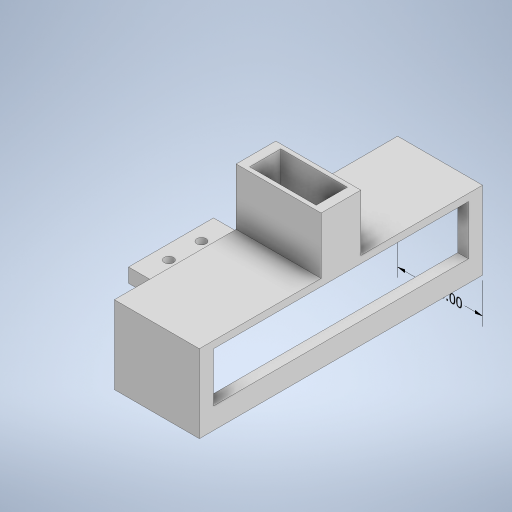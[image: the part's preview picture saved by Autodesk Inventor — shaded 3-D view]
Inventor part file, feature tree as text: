
AUTODESK INVENTOR PART (.ipt)
format: ipt  version: 2023 (Build 270158000, 158)  size: 323,584 bytes
history: native  units: mm
features: extrude x8, sketch x8, other x3, plane x1
ambient origin geometry x8: Origin, YZ Plane, XZ Plane, XY Plane, X Axis, Y Axis, Z Axis, Center Point
bodies: Body1 (feature_tree)
feature tree (20):
  other  "Sólido1"
  other  "Anotaciones"
  extrude  "Extrusión1"  Depth=200.0mm
  extrude  "Extrusión2"  Depth=45.0mm
  extrude  "Extrusión3"  TaperAngle=0.0deg  [1 undecoded]
  extrude  "Extrusión4"  Depth=10.0mm
  extrude  "Extrusión5"  Depth=10.0mm TaperAngle=0.0deg
  extrude  "Extrusión6"  Depth=60.0mm
  extrude  "Extrusión7"  Depth=6.5mm
  plane  "Plano de trabajo1"
  extrude  "Extrusión8"  Depth=18.5mm
  sketch  "Boceto2"  dims[d0=60.0mm d1=200.0mm]
  sketch  "Boceto3"  dims[d2=55.0mm d3=0.0mm d4=45.0mm]
  sketch  "Boceto4"  dims[d5=50.0mm d6=0.0mm]
  sketch  "Boceto5"  dims[d7=190.0mm d8=0.0mm d9=10.0mm]
  sketch  "Boceto6"  dims[d10=15.0mm d11=10.0mm d12=0.0mm]
  sketch  "Boceto7"  dims[d16=30.0mm d17=60.0mm]
  sketch  "Boceto8"  dims[d18=60.0mm d19=6.5mm]
  sketch  "Boceto10"  dims[d20=20.0mm d21=18.5mm d22=23.0mm d23=6.5mm d24=30.0mm d25=18.5mm d26=10.0mm d27=0.0mm d28=28.0mm d29=40.0mm d30=0.0mm d31=47.0mm d32=22.0mm d33=43.0mm d34=0.0mm d35=22.0mm d36=10.0mm d37=0.0mm d38=10.0mm d39=0.0mm d41=0.0mm d42=15.0mm d43=0.0mm d13=0.760408mm d14=1.168497mm d15=60.0mm]
  other  "Cota lineal 1"
note: 1 required parameter value undecoded (feature->parameter linkage not recoverable at this tier; creation-order binding heuristic only, values carry confidence <= 0.55)
